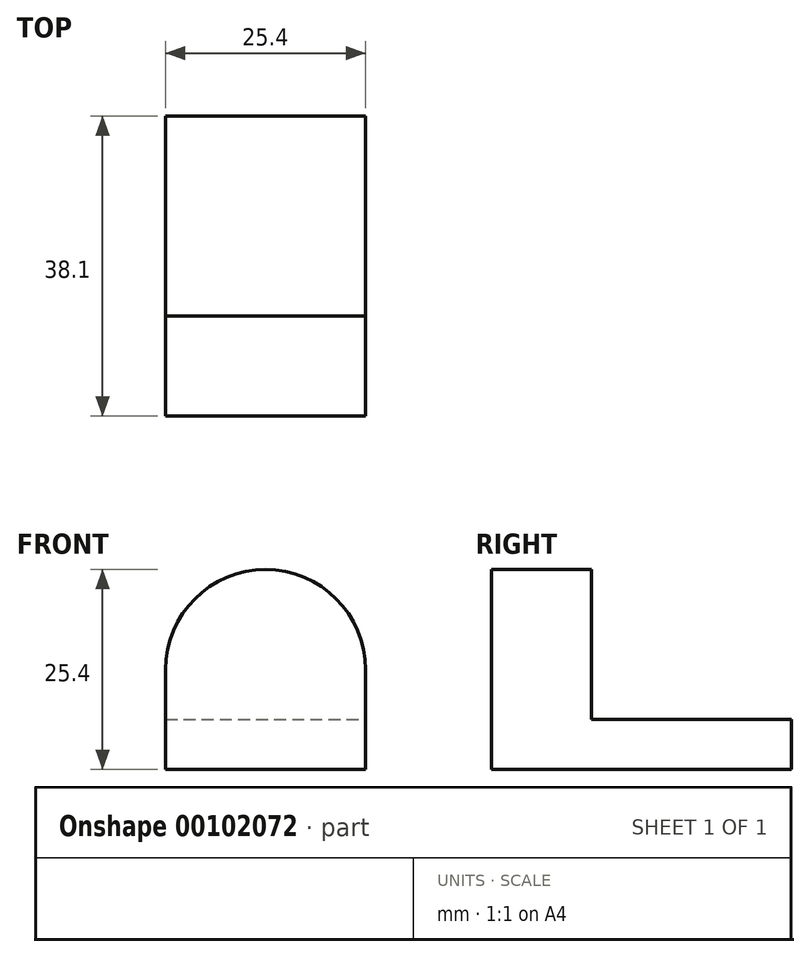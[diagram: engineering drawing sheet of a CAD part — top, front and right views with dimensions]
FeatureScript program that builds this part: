
annotation { "Feature Type Name" : "Feature", "Feature Type Description" : "" }
export const myFeature = defineFeature(function(context is Context, id is Id, definition is map)
    precondition{}
    {
        {
            var Q0;
            Q0=qCreatedBy(makeId("Front.planeOp"),FACE);
            var sketch = newSketch(context, id + "F0", { "sketchPlane" : qUnion([Q0])});
            skLineSegment(sketch, "E0", {"start": v(0, 0) * mm, "end": v(25.4, 0) * mm});
            skLineSegment(sketch, "E1", {"start": v(25.4, 0) * mm, "end": v(25.4, 12.7) * mm});
            skLineSegment(sketch, "E2", {"start": v(0, 12.7) * mm, "end": v(0, 0) * mm});
            skArc(sketch, "E3", {"start": v(0, 12.7) * mm, "mid": v(12.7, 25.4) * mm, "end": v(25.4, 12.7) * mm});
            skSolve(sketch);
        }
        {
            var Q0;
            Q0 = qSketchRegion(id + "F0", true);
            extrude(context, id + "F1", {"entities" : qUnion([Q0]), "depth" : 38.1 * mm});
        }
        {
            var Q0;
            Q0=qCreatedBy(makeId("Front.planeOp"),FACE);
            var sketch = newSketch(context, id + "F2", { "sketchPlane" : qUnion([Q0])});
            skLineSegment(sketch, "E4", {"start": v(0, 6.35) * mm, "end": v(25.4, 6.35) * mm});
            skLineSegment(sketch, "E5", {"start": v(0, 6.35) * mm, "end": v(0, 12.7) * mm});
            skLineSegment(sketch, "E6", {"start": v(25.4, 6.35) * mm, "end": v(25.4, 12.7) * mm});
            skArc(sketch, "E7", {"start": v(0, 12.7) * mm, "mid": v(12.7, 25.4) * mm, "end": v(25.4, 12.7) * mm});
            skSolve(sketch);
        }
        {
            var Q0;
            Q0 = qSketchRegion(id + "F2", true);
            extrude(context, id + "F3", {"entities" : qUnion([Q0]), "operationType" : NewBodyOperationType.REMOVE, "depth" : 25.4 * mm});
        }
    });
